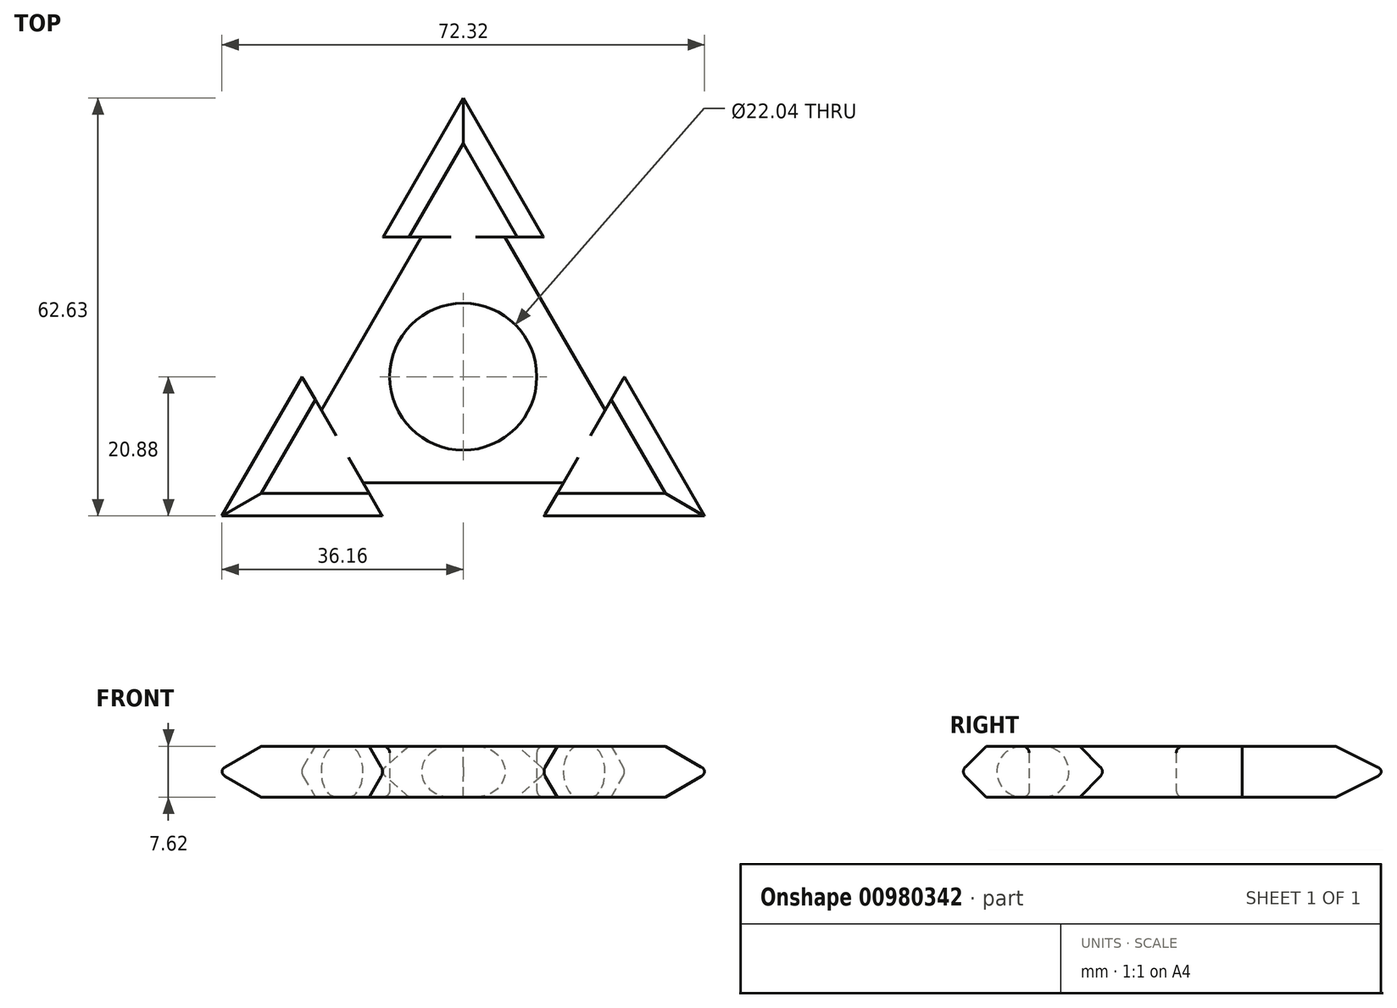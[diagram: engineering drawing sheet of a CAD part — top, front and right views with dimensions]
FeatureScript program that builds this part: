
annotation { "Feature Type Name" : "Feature", "Feature Type Description" : "" }
export const myFeature = defineFeature(function(context is Context, id is Id, definition is map)
    precondition{}
    {
        {
            var Q0;
            Q0=qCreatedBy(makeId("Top.planeOp"),FACE);
            var sketch = newSketch(context, id + "F0", { "sketchPlane" : qUnion([Q0])});
            skLineSegment(sketch, "E0", {"start": v(0, 42.58) * mm, "end": v(-12.5, 20.93) * mm});
            skLineSegment(sketch, "E1", {"start": v(-36.87, -21.29) * mm, "end": v(-11.87, -21.29) * mm});
            skLineSegment(sketch, "E2", {"start": v(36.87, -21.29) * mm, "end": v(24.37, 0.36) * mm});
            skLineSegment(sketch, "E3", {"start": v(-24.37, 0.36) * mm, "end": v(-18.12, -10.46) * mm});
            skLineSegment(sketch, "E4", {"start": v(0, 20.93) * mm, "end": v(-12.5, 20.93) * mm});
            skLineSegment(sketch, "E5", {"start": v(18.13, -10.46) * mm, "end": v(11.88, -21.29) * mm});
            skLineSegment(sketch, "E6", {"start": v(-11.88, -21.29) * mm, "end": v(-18.12, -10.46) * mm});
            skLineSegment(sketch, "E7", {"start": v(0, 20.93) * mm, "end": v(12.5, 20.93) * mm});
            skLineSegment(sketch, "E8", {"start": v(24.37, 0.36) * mm, "end": v(18.12, -10.46) * mm});
            skLineSegment(sketch, "E9", {"start": v(0, 42.58) * mm, "end": v(0, 20.93) * mm, "construction": true});
            skLineSegment(sketch, "E10", {"start": v(-36.87, -21.29) * mm, "end": v(-18.13, -10.46) * mm, "construction": true});
            skLineSegment(sketch, "E11", {"start": v(18.13, -10.46) * mm, "end": v(36.87, -21.29) * mm, "construction": true});
            skLineSegment(sketch, "E12", {"start": v(-6.25, 20.93) * mm, "end": v(-21.25, -5.05) * mm});
            skLineSegment(sketch, "E13", {"start": v(-15, -15.88) * mm, "end": v(15, -15.88) * mm});
            skLineSegment(sketch, "E14", {"start": v(21.25, -5.05) * mm, "end": v(6.25, 20.93) * mm});
            skLineSegment(sketch, "E15.trimOffspring", {"start": v(-24.37, 0.36) * mm, "end": v(-36.88, -21.29) * mm});
            skPoint(sketch, "E16.orphan", {"position": v(-27.5, -15.88) * mm});
            skLineSegment(sketch, "E17.trimOffspring", {"start": v(11.88, -21.29) * mm, "end": v(36.87, -21.29) * mm});
            skLineSegment(sketch, "E18.trimOffspring", {"start": v(12.5, 20.93) * mm, "end": v(0, 42.58) * mm});
            skPoint(sketch, "E19.orphan", {"position": v(0, 31.75) * mm});
            skLineSegment(sketch, "E20", {"start": v(0, 0) * mm, "end": v(0, 20.93) * mm, "construction": true});
            skLineSegment(sketch, "E21", {"start": v(0, 0) * mm, "end": v(18.12, -10.46) * mm, "construction": true});
            skLineSegment(sketch, "E22", {"start": v(0, 0) * mm, "end": v(-18.12, -10.46) * mm, "construction": true});
            skCircle(sketch, "E23", {"center": v(0, 0) * mm, "radius": 11.02 * mm});
            skSolve(sketch);
        }
        {
            var Q0;
            {var subQ10=sQuery(id+"F0.wireOp",EDGE,"E12");Q0=makeQuery(id+"F0.imprint","IMPRINT",FACE,{"disambiguationData":[TD([[makeQuery(id+"F0.imprint","IMPRINT",EDGE,{"derivedFrom":subQ10}),1.0]])]});}
            var Q1;
            {var subQ1=sQuery(id+"F0.wireOp",EDGE,"E1");Q1=makeQuery(id+"F0.imprint","IMPRINT",FACE,{"disambiguationData":[TD([[makeQuery(id+"F0.imprint","IMPRINT",EDGE,{"derivedFrom":subQ1}),1.0]])]});}
            var Q2;
            {var subQ1=sQuery(id+"F0.wireOp",EDGE,"E2");Q2=makeQuery(id+"F0.imprint","IMPRINT",FACE,{"disambiguationData":[TD([[makeQuery(id+"F0.imprint","IMPRINT",EDGE,{"derivedFrom":subQ1}),1.0]])]});}
            var Q3;
            {var subQ4=sQuery(id+"F0.wireOp",EDGE,"E0");Q3=makeQuery(id+"F0.imprint","IMPRINT",FACE,{"disambiguationData":[TD([[makeQuery(id+"F0.imprint","IMPRINT",EDGE,{"derivedFrom":subQ4}),1.0]])]});}
            extrude(context, id + "F1", {"entities" : qUnion([Q0, Q1, Q2, Q3]), "depth" : 7.62 * mm, "offsetDistance" : 25 * mm});
        }
        {
            var Q0;
            Q0=makeQuery(id+"F1.opExtrude","CAP_EDGE",EDGE,{"disambiguationData":[OSD([sQuery(id+"F0.wireOp",EDGE,"E1")])],"isStart":false});
            var Q1;
            Q1=makeQuery(id+"F1.opExtrude","CAP_EDGE",EDGE,{"disambiguationData":[OSD([sQuery(id+"F0.wireOp",EDGE,"E1")])],"isStart":true});
            var Q2;
            Q2=makeQuery(id+"F1.opExtrude","CAP_EDGE",EDGE,{"disambiguationData":[OSD([sQuery(id+"F0.wireOp",EDGE,"E2")])],"isStart":false});
            var Q3;
            Q3=makeQuery(id+"F1.opExtrude","CAP_EDGE",EDGE,{"disambiguationData":[OSD([sQuery(id+"F0.wireOp",EDGE,"E2")])],"isStart":true});
            var Q4;
            Q4=makeQuery(id+"F1.opExtrude","CAP_EDGE",EDGE,{"disambiguationData":[OSD([sQuery(id+"F0.wireOp",EDGE,"E15.trimOffspring")])],"isStart":false});
            var Q5;
            Q5=makeQuery(id+"F1.opExtrude","CAP_EDGE",EDGE,{"disambiguationData":[OSD([sQuery(id+"F0.wireOp",EDGE,"E15.trimOffspring")])],"isStart":true});
            var Q6;
            Q6=makeQuery(id+"F1.opExtrude","CAP_EDGE",EDGE,{"disambiguationData":[OSD([sQuery(id+"F0.wireOp",EDGE,"E17.trimOffspring")])],"isStart":false});
            var Q7;
            Q7=makeQuery(id+"F1.opExtrude","CAP_EDGE",EDGE,{"disambiguationData":[OSD([sQuery(id+"F0.wireOp",EDGE,"E17.trimOffspring")])],"isStart":true});
            var Q8;
            Q8=makeQuery(id+"F1.opExtrude","CAP_EDGE",EDGE,{"disambiguationData":[OSD([sQuery(id+"F0.wireOp",EDGE,"E0")])],"isStart":false});
            var Q9;
            Q9=makeQuery(id+"F1.opExtrude","CAP_EDGE",EDGE,{"disambiguationData":[OSD([sQuery(id+"F0.wireOp",EDGE,"E0")])],"isStart":true});
            var Q10;
            Q10=makeQuery(id+"F1.opExtrude","CAP_EDGE",EDGE,{"disambiguationData":[OSD([sQuery(id+"F0.wireOp",EDGE,"E18.trimOffspring")])],"isStart":false});
            var Q11;
            Q11=makeQuery(id+"F1.opExtrude","CAP_EDGE",EDGE,{"disambiguationData":[OSD([sQuery(id+"F0.wireOp",EDGE,"E18.trimOffspring")])],"isStart":true});
            chamfer(context, id + "F2", {"entities" : qUnion([Q0, Q1, Q2, Q3, Q4, Q5, Q6, Q7, Q8, Q9, Q10, Q11]), "width" : 3.81 * mm, "tangentPropagation" : true});
        }
        {
            var Q0;
            Q0=makeQuery(id+"F1.opExtrude","CAP_EDGE",EDGE,{"disambiguationData":[OSD([sQuery(id+"F0.wireOp",EDGE,"E14")])],"isStart":false});
            var Q1;
            Q1=makeQuery(id+"F1.opExtrude","CAP_EDGE",EDGE,{"disambiguationData":[OSD([sQuery(id+"F0.wireOp",EDGE,"E14")])],"isStart":true});
            var Q2;
            Q2=makeQuery(id+"F1.opExtrude","CAP_EDGE",EDGE,{"disambiguationData":[OSD([sQuery(id+"F0.wireOp",EDGE,"E12")])],"isStart":false});
            var Q3;
            Q3=makeQuery(id+"F1.opExtrude","CAP_EDGE",EDGE,{"disambiguationData":[OSD([sQuery(id+"F0.wireOp",EDGE,"E12")])],"isStart":true});
            var Q4;
            Q4=makeQuery(id+"F1.opExtrude","CAP_EDGE",EDGE,{"disambiguationData":[OSD([sQuery(id+"F0.wireOp",EDGE,"E13")])],"isStart":false});
            var Q5;
            Q5=makeQuery(id+"F1.opExtrude","CAP_EDGE",EDGE,{"disambiguationData":[OSD([sQuery(id+"F0.wireOp",EDGE,"E13")])],"isStart":true});
            fillet(context, id + "F3", {"entities" : qUnion([Q0, Q1, Q2, Q3, Q4, Q5]), "radius" : 3.81 * mm, "tangentPropagation" : true, "allowEdgeOverflow" : false});
        }
        {
            var Q0;
            Q0=makeQuery(id+"F1.opExtrude","CAP_EDGE",EDGE,{"disambiguationData":[OSD([sQuery(id+"F0.wireOp",EDGE,"E23")])],"isStart":false});
            var Q1;
            Q1=makeQuery(id+"F1.opExtrude","CAP_EDGE",EDGE,{"disambiguationData":[OSD([sQuery(id+"F0.wireOp",EDGE,"E23")])],"isStart":true});
            fillet(context, id + "F4", {"entities" : qUnion([Q0, Q1]), "radius" : 1 * mm, "tangentPropagation" : true, "allowEdgeOverflow" : false});
        }
        {
            var Q0;
            {var subQ0=sQuery(id+"F0.wireOp",EDGE,"E17.trimOffspring");Q0=makeQuery(id+"F2.opChamfer","BLEND_EDGE",EDGE,{"blendedFrom":[makeQuery(id+"F1.opExtrude","CAP_EDGE",EDGE,{"disambiguationData":[OSD([subQ0])],"isStart":true}),makeQuery(id+"F1.opExtrude","CAP_EDGE",EDGE,{"disambiguationData":[OSD([subQ0])],"isStart":false})],"blendedInto":[]});}
            var Q1;
            {var subQ0=sQuery(id+"F0.wireOp",EDGE,"E2");Q1=makeQuery(id+"F2.opChamfer","BLEND_EDGE",EDGE,{"blendedFrom":[makeQuery(id+"F1.opExtrude","CAP_EDGE",EDGE,{"disambiguationData":[OSD([subQ0])],"isStart":true}),makeQuery(id+"F1.opExtrude","CAP_EDGE",EDGE,{"disambiguationData":[OSD([subQ0])],"isStart":false})],"blendedInto":[]});}
            var Q2;
            {var subQ0=sQuery(id+"F0.wireOp",EDGE,"E18.trimOffspring");Q2=makeQuery(id+"F2.opChamfer","BLEND_EDGE",EDGE,{"blendedFrom":[makeQuery(id+"F1.opExtrude","CAP_EDGE",EDGE,{"disambiguationData":[OSD([subQ0])],"isStart":true}),makeQuery(id+"F1.opExtrude","CAP_EDGE",EDGE,{"disambiguationData":[OSD([subQ0])],"isStart":false})],"blendedInto":[]});}
            var Q3;
            {var subQ0=sQuery(id+"F0.wireOp",EDGE,"E0");Q3=makeQuery(id+"F2.opChamfer","BLEND_EDGE",EDGE,{"blendedFrom":[makeQuery(id+"F1.opExtrude","CAP_EDGE",EDGE,{"disambiguationData":[OSD([subQ0])],"isStart":true}),makeQuery(id+"F1.opExtrude","CAP_EDGE",EDGE,{"disambiguationData":[OSD([subQ0])],"isStart":false})],"blendedInto":[]});}
            var Q4;
            {var subQ0=sQuery(id+"F0.wireOp",EDGE,"E15.trimOffspring");Q4=makeQuery(id+"F2.opChamfer","BLEND_EDGE",EDGE,{"blendedFrom":[makeQuery(id+"F1.opExtrude","CAP_EDGE",EDGE,{"disambiguationData":[OSD([subQ0])],"isStart":true}),makeQuery(id+"F1.opExtrude","CAP_EDGE",EDGE,{"disambiguationData":[OSD([subQ0])],"isStart":false})],"blendedInto":[]});}
            var Q5;
            {var subQ0=sQuery(id+"F0.wireOp",EDGE,"E1");Q5=makeQuery(id+"F2.opChamfer","BLEND_EDGE",EDGE,{"blendedFrom":[makeQuery(id+"F1.opExtrude","CAP_EDGE",EDGE,{"disambiguationData":[OSD([subQ0])],"isStart":true}),makeQuery(id+"F1.opExtrude","CAP_EDGE",EDGE,{"disambiguationData":[OSD([subQ0])],"isStart":false})],"blendedInto":[]});}
            fillet(context, id + "F5", {"entities" : qUnion([Q0, Q1, Q2, Q3, Q4, Q5]), "radius" : 1 * mm, "tangentPropagation" : true, "allowEdgeOverflow" : false});
        }
    });
